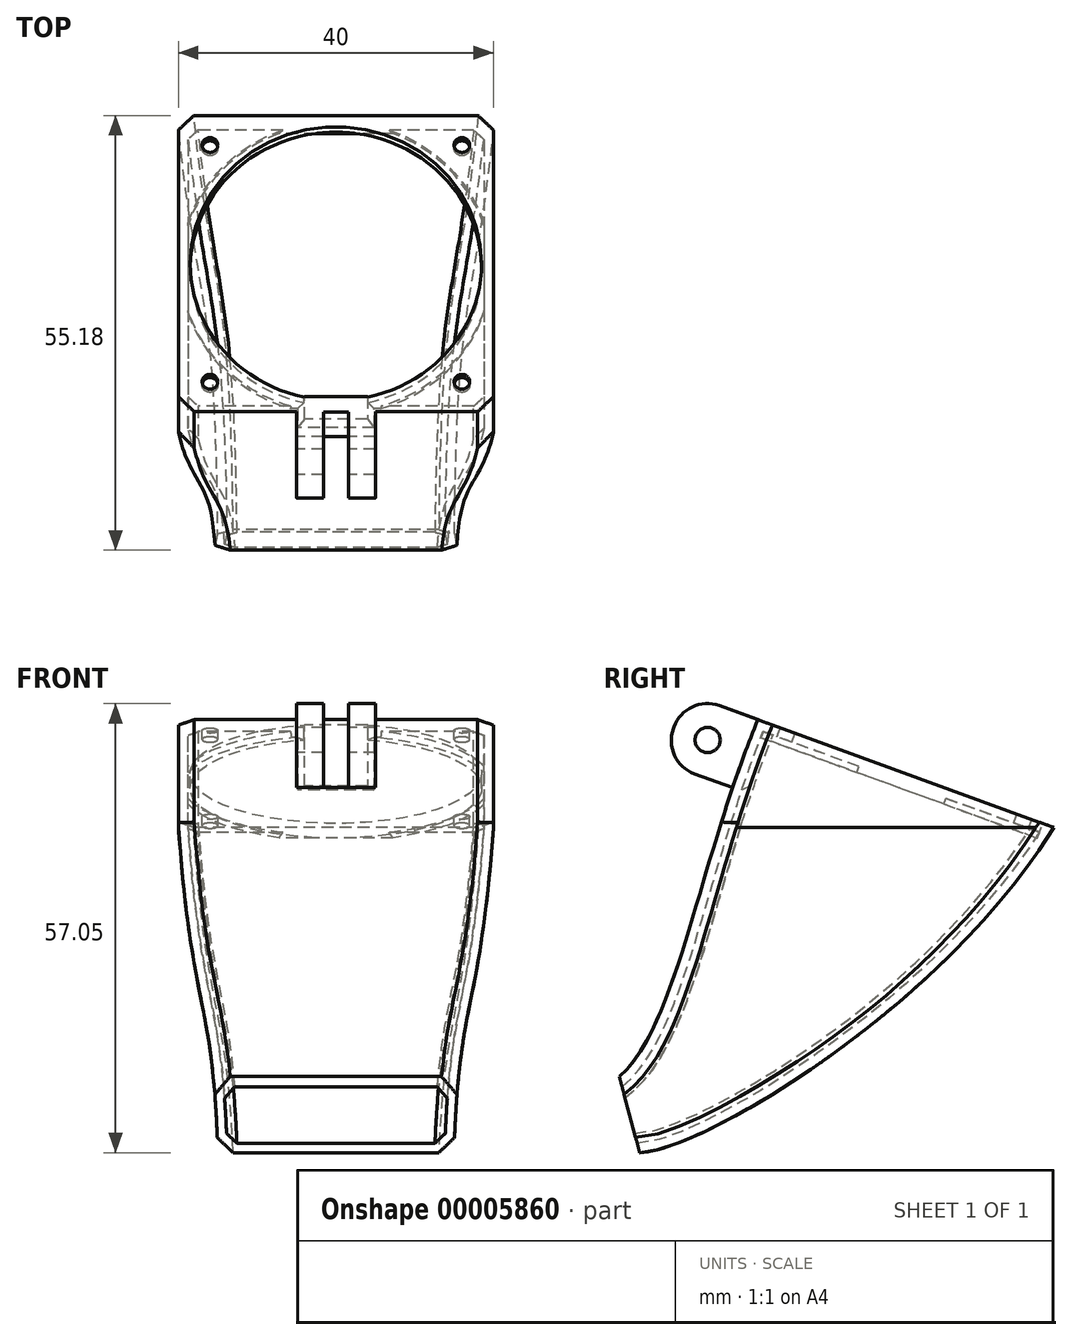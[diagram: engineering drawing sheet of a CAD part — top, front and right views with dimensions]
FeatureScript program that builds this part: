
annotation { "Feature Type Name" : "Feature", "Feature Type Description" : "" }
export const myFeature = defineFeature(function(context is Context, id is Id, definition is map)
    precondition{}
    {
        {
            var Q0;
            Q0=qCreatedBy(makeId("Right.planeOp"),FACE);
            var sketch = newSketch(context, id + "F0", { "sketchPlane" : qUnion([Q0])});
            skLineSegment(sketch, "E0", {"start": v(-2.59, 9.66) * mm, "end": v(0, 0) * mm});
            skLineSegment(sketch, "E1", {"start": v(52.59, 41.32) * mm, "end": v(15, 55) * mm});
            skFitSpline(sketch, "E2", {"points": [v(52.59, 41.32) * mm, v(0, 0) * mm], "startDerivative": vector(-42.87, -69.92) * mm, "endDerivative": vector(-21.77, 0) * mm});
            skFitSpline(sketch, "E3", {"points": [v(15, 55) * mm, v(-2.59, 9.66) * mm], "startDerivative": vector(-23.12, -56.46) * mm, "endDerivative": vector(-21.93, -19.1) * mm});
            skSolve(sketch);
        }
        {
            var Q0;
            Q0 = qSketchRegion(id + "F0", true);
            extrude(context, id + "F1", {"entities" : qUnion([Q0]), "endBound" : BoundingType.SYMMETRIC, "depth" : 40 * mm});
        }
        {
            var Q0;
            Q0=qCreatedBy(makeId("Front.planeOp"),FACE);
            var sketch = newSketch(context, id + "F2", { "sketchPlane" : qUnion([Q0])});
            skLineSegment(sketch, "E4", {"start": v(15, 0) * mm, "end": v(-15, 0) * mm});
            skLineSegment(sketch, "E5", {"start": v(20, 55) * mm, "end": v(-20, 55) * mm});
            skLineSegment(sketch, "E6", {"start": v(-20, 55) * mm, "end": v(-20, 41.32) * mm});
            skLineSegment(sketch, "E7", {"start": v(20, 55) * mm, "end": v(20, 41.32) * mm});
            skPoint(sketch, "E8", {"position": v(0, 0) * mm});
            skFitSpline(sketch, "E9", {"points": [v(20, 41.32) * mm, v(15, 0) * mm], "startDerivative": vector(-5.16, -71.52) * mm, "endDerivative": vector(-1.89, -60.47) * mm});
            skFitSpline(sketch, "E10.0.MirrorCS", {"points": [v(-20, 41.32) * mm, v(-15, 0) * mm], "startDerivative": vector(5.16, -71.52) * mm, "endDerivative": vector(1.89, -60.47) * mm});
            skSolve(sketch);
        }
        {
            var Q0;
            Q0=makeQuery(id+"F2.imprint","IMPRINT",FACE,{"disambiguationData":[TD([[makeQuery(id+"F2.imprint","IMPRINT",EDGE,{"derivedFrom":sQuery(id+"F2.wireOp",EDGE,"E4")}),-1.0]])]});
            var Q1;
            Q1=makeQuery(id+"F1.opExtrude","SWEPT_FACE",FACE,{"disambiguationData":[OSD([sQuery(id+"F0.wireOp",EDGE,"E2")])]});
            extrude(context, id + "F3", {"entities" : qUnion([Q0]), "operationType" : NewBodyOperationType.INTERSECT, "endBound" : BoundingType.THROUGH_ALL, "oppositeDirection" : true, "endBoundEntityBody" : qUnion([Q1]), "depth" : 25 * mm, "hasSecondDirection" : true, "secondDirectionOppositeDirection" : false, "secondDirectionDepth" : 10 * mm});
        }
        {
            var Q0;
            Q0=makeQuery(id+"F1.opExtrude","SWEPT_FACE",FACE,{"disambiguationData":[OSD([sQuery(id+"F0.wireOp",EDGE,"E1")])]});
            var sketch = newSketch(context, id + "F4", { "sketchPlane" : qUnion([Q0])});
            skLineSegment(sketch, "E11", {"start": v(20, -4.72) * mm, "end": v(-20, 35.28) * mm, "construction": true});
            skLineSegment(sketch, "E12", {"start": v(-20, -4.72) * mm, "end": v(20, 35.28) * mm, "construction": true});
            skCircle(sketch, "E13", {"center": v(0, 15.28) * mm, "radius": 18.5 * mm});
            skSolve(sketch);
        }
        {
            var Q0;
            Q0 = qSketchRegion(id + "F4", true);
            extrude(context, id + "F5", {"entities" : qUnion([Q0]), "operationType" : NewBodyOperationType.REMOVE, "oppositeDirection" : true, "depth" : 2 * mm});
        }
        {
            var Q0;
            Q0=makeQuery(id+"F3.boolean.opBoolean","INTERSECT",EDGE,{"derivedFrom":[makeQuery(id+"F1.opExtrude","SWEPT_FACE",FACE,{"disambiguationData":[OSD([sQuery(id+"F0.wireOp",EDGE,"E3")])]}),makeQuery(id+"F3.opExtrude","SWEPT_FACE",FACE,{"disambiguationData":[OSD([sQuery(id+"F2.wireOp",EDGE,"E9")])]})]});
            var Q1;
            Q1=makeQuery(id+"F1.opExtrude","CAP_EDGE",EDGE,{"disambiguationData":[OSD([sQuery(id+"F0.wireOp",EDGE,"E3")])],"isStart":false});
            var Q2;
            Q2=makeQuery(id+"F3.boolean.opBoolean","INTERSECT",EDGE,{"derivedFrom":[makeQuery(id+"F1.opExtrude","SWEPT_FACE",FACE,{"disambiguationData":[OSD([sQuery(id+"F0.wireOp",EDGE,"E3")])]}),makeQuery(id+"F3.opExtrude","SWEPT_FACE",FACE,{"disambiguationData":[OSD([sQuery(id+"F2.wireOp",EDGE,"E10.0.MirrorCS")])]})]});
            var Q3;
            Q3=makeQuery(id+"F1.opExtrude","CAP_EDGE",EDGE,{"disambiguationData":[OSD([sQuery(id+"F0.wireOp",EDGE,"E3")])],"isStart":true});
            var Q4;
            Q4=makeQuery(id+"F3.boolean.opBoolean","INTERSECT",EDGE,{"derivedFrom":[makeQuery(id+"F1.opExtrude","SWEPT_FACE",FACE,{"disambiguationData":[OSD([sQuery(id+"F0.wireOp",EDGE,"E2")])]}),makeQuery(id+"F3.opExtrude","SWEPT_FACE",FACE,{"disambiguationData":[OSD([sQuery(id+"F2.wireOp",EDGE,"E9")])]})]});
            var Q5;
            Q5=makeQuery(id+"F3.boolean.opBoolean","INTERSECT",EDGE,{"derivedFrom":[makeQuery(id+"F1.opExtrude","SWEPT_FACE",FACE,{"disambiguationData":[OSD([sQuery(id+"F0.wireOp",EDGE,"E2")])]}),makeQuery(id+"F3.opExtrude","SWEPT_FACE",FACE,{"disambiguationData":[OSD([sQuery(id+"F2.wireOp",EDGE,"E10.0.MirrorCS")])]})]});
            chamfer(context, id + "F6", {"entities" : qUnion([Q0, Q1, Q2, Q3, Q4, Q5]), "width" : 2 * mm, "tangentPropagation" : true});
        }
        {
            var Q0;
            Q0=makeQuery(id+"F5.boolean.opBoolean","COPY",FACE,{"derivedFrom":makeQuery(id+"F5.opExtrude","CAP_FACE",FACE,{"disambiguationData":[OSD([sQuery(id+"F4.wireOp",EDGE,"E13")])],"isStart":false})});
            var Q1;
            Q1=makeQuery(id+"F1.opExtrude","SWEPT_FACE",FACE,{"disambiguationData":[OSD([sQuery(id+"F0.wireOp",EDGE,"E0")])]});
            shell(context, id + "F7", {"entities" : qUnion([Q0, Q1]), "thickness" : 1.2 * mm});
        }
        {
            var Q0;
            Q0=makeQuery(id+"F1.opExtrude","SWEPT_FACE",FACE,{"disambiguationData":[OSD([sQuery(id+"F0.wireOp",EDGE,"E1")])]});
            var sketch = newSketch(context, id + "F8", { "sketchPlane" : qUnion([Q0])});
            skCircle(sketch, "E14", {"center": v(16, 31.32) * mm, "radius": 1 * mm});
            skCircle(sketch, "E15", {"center": v(-16, 31.32) * mm, "radius": 1 * mm});
            skCircle(sketch, "E16", {"center": v(-16, -0.68) * mm, "radius": 1 * mm});
            skCircle(sketch, "E17", {"center": v(16, -0.68) * mm, "radius": 1 * mm});
            skPoint(sketch, "E18", {"position": v(-20, 15.32) * mm});
            skSolve(sketch);
        }
        {
            var Q0;
            Q0 = qSketchRegion(id + "F8", true);
            var Q1;
            Q1=makeQuery(id+"F7.opShell","OFFSET_FACE",FACE,{"disambiguationData":[OSD([sQuery(id+"F0.wireOp",EDGE,"E1")]),OD(1.0)]});
            extrude(context, id + "F9", {"entities" : qUnion([Q0]), "operationType" : NewBodyOperationType.REMOVE, "endBound" : BoundingType.UP_TO_SURFACE, "oppositeDirection" : true, "endBoundEntityFace" : qUnion([Q1]), "depth" : 25 * mm});
        }
        {
            var Q0;
            Q0=qCreatedBy(makeId("Right.planeOp"),FACE);
            var sketch = newSketch(context, id + "F10", { "sketchPlane" : qUnion([Q0])});
            skLineSegment(sketch, "E19", {"start": v(5.88, 58.32) * mm, "end": v(2.74, 49.67) * mm});
            skLineSegment(sketch, "E20", {"start": v(2.74, 49.67) * mm, "end": v(13.73, 45.67) * mm});
            skLineSegment(sketch, "E21", {"start": v(13.73, 45.67) * mm, "end": v(16.88, 54.32) * mm});
            skLineSegment(sketch, "E22", {"start": v(16.88, 54.32) * mm, "end": v(15, 55) * mm});
            skLineSegment(sketch, "E23", {"start": v(15, 55) * mm, "end": v(15, 55) * mm});
            skLineSegment(sketch, "E24", {"start": v(15, 55) * mm, "end": v(5.88, 58.32) * mm});
            skCircle(sketch, "E25", {"center": v(8.63, 52.42) * mm, "radius": 1.6 * mm});
            skSolve(sketch);
        }
        {
            var Q0;
            Q0 = qSketchRegion(id + "F10", true);
            extrude(context, id + "F11", {"entities" : qUnion([Q0]), "operationType" : NewBodyOperationType.ADD, "endBound" : BoundingType.SYMMETRIC, "depth" : 10 * mm});
        }
        {
            var Q0;
            Q0=makeQuery(id+"F11.opExtrude","CAP_EDGE",EDGE,{"disambiguationData":[OSD([sQuery(id+"F10.wireOp",EDGE,"E21")])],"isStart":true});
            var Q1;
            Q1=makeQuery(id+"F11.opExtrude","CAP_EDGE",EDGE,{"disambiguationData":[OSD([sQuery(id+"F10.wireOp",EDGE,"E21")])],"isStart":false});
            var Q2;
            Q2=makeQuery(id+"F11.opExtrude","SWEPT_EDGE",EDGE,{"disambiguationData":[OSD([sQuery(id+"F10.wireOp",EDGE,"E20"),sQuery(id+"F10.wireOp",EDGE,"E21")])]});
            chamfer(context, id + "F12", {"entities" : qUnion([Q0, Q1, Q2]), "width" : 1 * mm, "tangentPropagation" : true});
        }
        {
            var Q0;
            Q0=makeQuery(id+"F11.opExtrude","SWEPT_EDGE",EDGE,{"disambiguationData":[OSD([sQuery(id+"F10.wireOp",EDGE,"E19"),sQuery(id+"F10.wireOp",EDGE,"E20")])]});
            var Q1;
            Q1=makeQuery(id+"F11.opExtrude","SWEPT_EDGE",EDGE,{"disambiguationData":[OSD([sQuery(id+"F10.wireOp",EDGE,"E19"),sQuery(id+"F10.wireOp",EDGE,"E24")])]});
            fillet(context, id + "F13", {"entities" : qUnion([Q0, Q1]), "radius" : 4.5 * mm, "tangentPropagation" : true, "allowEdgeOverflow" : false});
        }
        {
            var Q0;
            {var subQ0=sQuery(id+"F10.wireOp",EDGE,"E20");Q0=makeQuery(id+"F11.boolean.opBoolean","SPLIT",FACE,{"disambiguationData":[TD([makeQuery(id+"F1.opExtrude","SWEPT_FACE",FACE,{"disambiguationData":[OSD([sQuery(id+"F0.wireOp",EDGE,"E3")])]})])],"derivedFrom":makeQuery(id+"F11.opExtrude","SWEPT_FACE",FACE,{"disambiguationData":[OSD([subQ0])]})});}
            var sketch = newSketch(context, id + "F14", { "sketchPlane" : qUnion([Q0])});
            skLineSegment(sketch, "E26.bottom", {"start": v(1.6, 17.33) * mm, "end": v(-1.6, 17.33) * mm});
            skLineSegment(sketch, "E26.top", {"start": v(1.6, 4.77) * mm, "end": v(-1.6, 4.77) * mm});
            skLineSegment(sketch, "E26.left", {"start": v(1.6, 17.33) * mm, "end": v(1.6, 4.77) * mm});
            skLineSegment(sketch, "E26.right", {"start": v(-1.6, 17.33) * mm, "end": v(-1.6, 4.77) * mm});
            skPoint(sketch, "E27", {"position": v(0, 17.33) * mm});
            skSolve(sketch);
        }
        {
            var Q0;
            Q0 = qSketchRegion(id + "F14", true);
            var Q1;
            Q1=makeQuery(id+"F11.boolean.opBoolean","MERGE",FACE,{"derivedFrom":[makeQuery(id+"F1.opExtrude","SWEPT_FACE",FACE,{"disambiguationData":[OSD([sQuery(id+"F0.wireOp",EDGE,"E1")])]}),makeQuery(id+"F11.opExtrude","SWEPT_FACE",FACE,{"disambiguationData":[OSD([sQuery(id+"F10.wireOp",EDGE,"E22"),sQuery(id+"F10.wireOp",EDGE,"E24")])]})]});
            extrude(context, id + "F15", {"entities" : qUnion([Q0]), "operationType" : NewBodyOperationType.REMOVE, "endBound" : BoundingType.UP_TO_SURFACE, "oppositeDirection" : true, "endBoundEntityFace" : qUnion([Q1]), "depth" : 25 * mm});
        }
    });
